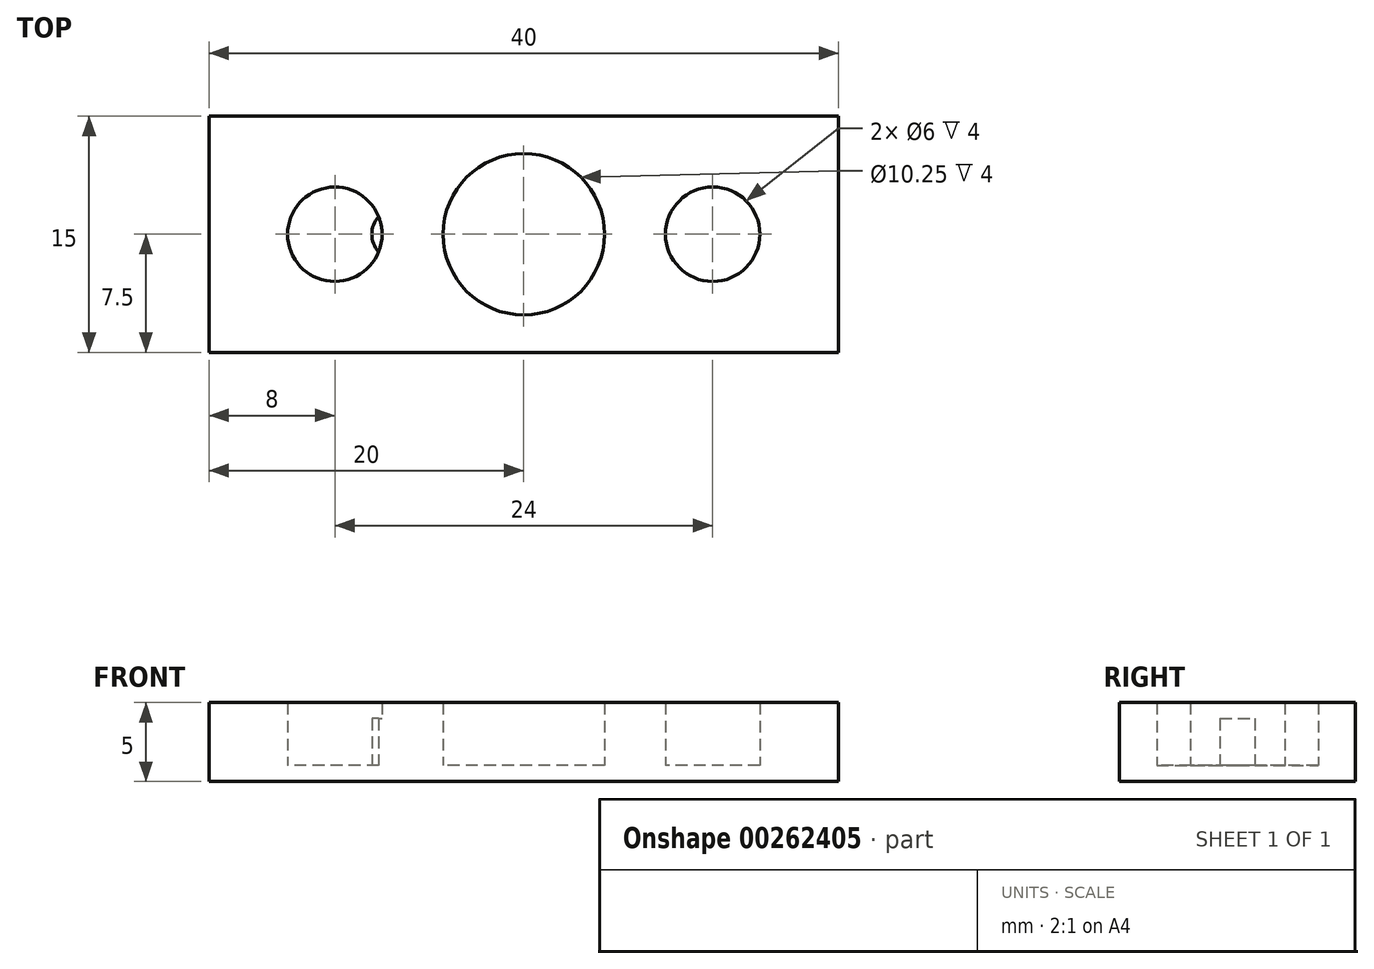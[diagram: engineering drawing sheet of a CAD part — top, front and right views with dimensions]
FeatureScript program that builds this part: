
annotation { "Feature Type Name" : "Feature", "Feature Type Description" : "" }
export const myFeature = defineFeature(function(context is Context, id is Id, definition is map)
    precondition{}
    {
        {
            var Q0;
            Q0=qCreatedBy(makeId("Top.planeOp"),FACE);
            var sketch = newSketch(context, id + "F0", { "sketchPlane" : qUnion([Q0])});
            skLineSegment(sketch, "E0.bottom", {"start": v(20, -7.5) * mm, "end": v(-20, -7.5) * mm});
            skLineSegment(sketch, "E0.top", {"start": v(20, 7.5) * mm, "end": v(-20, 7.5) * mm});
            skLineSegment(sketch, "E0.left", {"start": v(20, -7.5) * mm, "end": v(20, 7.5) * mm});
            skLineSegment(sketch, "E0.right", {"start": v(-20, -7.5) * mm, "end": v(-20, 7.5) * mm});
            skPoint(sketch, "E0.middle", {"position": v(0, 0) * mm});
            skCircle(sketch, "E1", {"center": v(0, 0) * mm, "radius": 3 * mm});
            skCircle(sketch, "E2", {"center": v(0, 0) * mm, "radius": 5.12 * mm});
            skCircle(sketch, "E3", {"center": v(-12, 0) * mm, "radius": 5.25 * mm, "construction": true});
            skCircle(sketch, "E4", {"center": v(-12, 0) * mm, "radius": 3 * mm});
            skCircle(sketch, "E5", {"center": v(12, 0) * mm, "radius": 5 * mm, "construction": true});
            skCircle(sketch, "E6", {"center": v(12, 0) * mm, "radius": 3 * mm});
            skSolve(sketch);
        }
        {
            var Q0;
            Q0=makeQuery(id+"F0.imprint","IMPRINT",FACE,{"disambiguationData":[TD([[makeQuery(id+"F0.imprint","IMPRINT",EDGE,{"derivedFrom":sQuery(id+"F0.wireOp",EDGE,"E0.bottom")}),-1.0]])]});
            var Q1;
            Q1=makeQuery(id+"F0.imprint","IMPRINT",FACE,{"disambiguationData":[TD([[makeQuery(id+"F0.imprint","IMPRINT",EDGE,{"derivedFrom":sQuery(id+"F0.wireOp",EDGE,"E3")}),1.0]])]});
            var Q2;
            Q2=makeQuery(id+"F0.imprint","IMPRINT",FACE,{"disambiguationData":[TD([[makeQuery(id+"F0.imprint","IMPRINT",EDGE,{"derivedFrom":sQuery(id+"F0.wireOp",EDGE,"E1")}),-1.0]])]});
            var Q3;
            Q3=makeQuery(id+"F0.imprint","IMPRINT",FACE,{"disambiguationData":[TD([[makeQuery(id+"F0.imprint","IMPRINT",EDGE,{"derivedFrom":sQuery(id+"F0.wireOp",EDGE,"E5")}),1.0]])]});
            extrude(context, id + "F1", {"entities" : qUnion([Q0, Q1, Q2, Q3]), "depth" : 1 * mm});
        }
        {
            var Q0;
            Q0=makeQuery(id+"F0.imprint","IMPRINT",FACE,{"disambiguationData":[TD([[makeQuery(id+"F0.imprint","IMPRINT",EDGE,{"derivedFrom":sQuery(id+"F0.wireOp",EDGE,"E0.bottom")}),-1.0]])]});
            extrude(context, id + "F2", {"entities" : qUnion([Q0]), "operationType" : NewBodyOperationType.ADD, "depth" : 5 * mm});
        }
        {
            var Q0;
            Q0=qCreatedBy(makeId("Top.planeOp"),FACE);
            var sketch = newSketch(context, id + "F3", { "sketchPlane" : qUnion([Q0])});
            skLineSegment(sketch, "E7.bottom", {"start": v(20, -5) * mm, "end": v(-20, -5) * mm});
            skLineSegment(sketch, "E7.top", {"start": v(20, 5) * mm, "end": v(-20, 5) * mm});
            skLineSegment(sketch, "E7.left", {"start": v(20, -5) * mm, "end": v(20, 5) * mm});
            skLineSegment(sketch, "E7.right", {"start": v(-20, -5) * mm, "end": v(-20, 5) * mm});
            skPoint(sketch, "E7.middle", {"position": v(0, 0) * mm});
            skCircle(sketch, "E8", {"center": v(0, 0) * mm, "radius": 1.6 * mm, "construction": true});
            skCircle(sketch, "E9", {"center": v(8, 0) * mm, "radius": 1.55 * mm, "construction": true});
            skCircle(sketch, "E10", {"center": v(-8, 0) * mm, "radius": 1.65 * mm});
            skCircle(sketch, "E11", {"center": v(-16, 0) * mm, "radius": 1.7 * mm, "construction": true});
            skCircle(sketch, "E12", {"center": v(16, 0) * mm, "radius": 1.5 * mm, "construction": true});
            skSolve(sketch);
        }
        {
            var Q0;
            Q0=makeQuery(id+"F3.imprint","IMPRINT",FACE,{"disambiguationData":[TD([[makeQuery(id+"F3.imprint","IMPRINT",EDGE,{"derivedFrom":sQuery(id+"F3.wireOp",EDGE,"E7.bottom")}),-1.0]])]});
            var Q1;
            Q1=makeQuery(id+"F3.imprint","IMPRINT",FACE,{"disambiguationData":[TD([[makeQuery(id+"F3.imprint","IMPRINT",EDGE,{"derivedFrom":sQuery(id+"F3.wireOp",EDGE,"E11")}),1.0]])]});
            var Q2;
            Q2=makeQuery(id+"F3.imprint","IMPRINT",FACE,{"disambiguationData":[TD([[makeQuery(id+"F3.imprint","IMPRINT",EDGE,{"derivedFrom":sQuery(id+"F3.wireOp",EDGE,"E10")}),1.0]])]});
            var Q3;
            Q3=makeQuery(id+"F3.imprint","IMPRINT",FACE,{"disambiguationData":[TD([[makeQuery(id+"F3.imprint","IMPRINT",EDGE,{"derivedFrom":sQuery(id+"F3.wireOp",EDGE,"E8")}),1.0]])]});
            var Q4;
            Q4=makeQuery(id+"F3.imprint","IMPRINT",FACE,{"disambiguationData":[TD([[makeQuery(id+"F3.imprint","IMPRINT",EDGE,{"derivedFrom":sQuery(id+"F3.wireOp",EDGE,"E9")}),1.0]])]});
            var Q5;
            Q5=makeQuery(id+"F3.imprint","IMPRINT",FACE,{"disambiguationData":[TD([[makeQuery(id+"F3.imprint","IMPRINT",EDGE,{"derivedFrom":sQuery(id+"F3.wireOp",EDGE,"E12")}),1.0]])]});
            extrude(context, id + "F4", {"entities" : qUnion([Q0, Q1, Q2, Q3, Q4, Q5]), "depth" : 1 * mm});
        }
        {
            var Q0;
            Q0=makeQuery(id+"F3.imprint","IMPRINT",FACE,{"disambiguationData":[TD([[makeQuery(id+"F3.imprint","IMPRINT",EDGE,{"derivedFrom":sQuery(id+"F3.wireOp",EDGE,"E11")}),1.0]])]});
            var Q1;
            Q1=makeQuery(id+"F3.imprint","IMPRINT",FACE,{"disambiguationData":[TD([[makeQuery(id+"F3.imprint","IMPRINT",EDGE,{"derivedFrom":sQuery(id+"F3.wireOp",EDGE,"E10")}),1.0]])]});
            var Q2;
            Q2=makeQuery(id+"F3.imprint","IMPRINT",FACE,{"disambiguationData":[TD([[makeQuery(id+"F3.imprint","IMPRINT",EDGE,{"derivedFrom":sQuery(id+"F3.wireOp",EDGE,"E8")}),1.0]])]});
            var Q3;
            Q3=makeQuery(id+"F3.imprint","IMPRINT",FACE,{"disambiguationData":[TD([[makeQuery(id+"F3.imprint","IMPRINT",EDGE,{"derivedFrom":sQuery(id+"F3.wireOp",EDGE,"E9")}),1.0]])]});
            var Q4;
            Q4=makeQuery(id+"F3.imprint","IMPRINT",FACE,{"disambiguationData":[TD([[makeQuery(id+"F3.imprint","IMPRINT",EDGE,{"derivedFrom":sQuery(id+"F3.wireOp",EDGE,"E12")}),1.0]])]});
            extrude(context, id + "F5", {"entities" : qUnion([Q0, Q1, Q2, Q3, Q4]), "operationType" : NewBodyOperationType.ADD, "depth" : 4 * mm});
        }
    });
